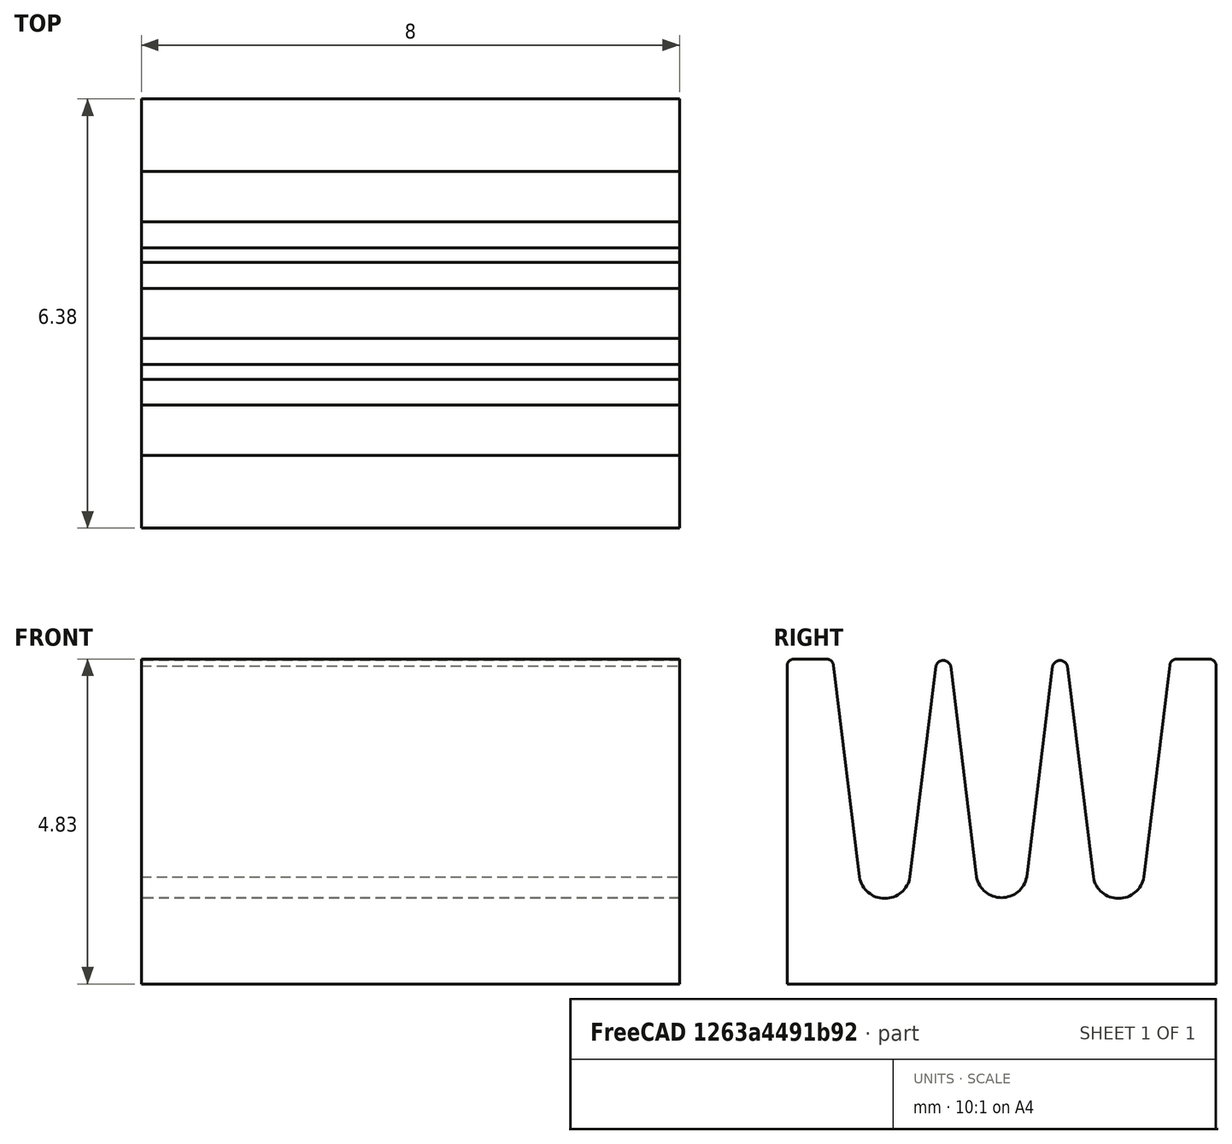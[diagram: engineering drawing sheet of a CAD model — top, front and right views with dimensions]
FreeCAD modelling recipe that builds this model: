
FCSTD DOCUMENT  (FreeCAD 0.14R3702 (Git))
Label: heat-sink-8x6x5mm
License: CC-BY 3.0
LicenseURL: http://creativecommons.org/licenses/by/3.0/
objects: Sketcher::SketchObject×1, PartDesign::Pad×1
note: 3 computed .brp shape members not serialized (recipe doc carries the construction recipe); baked Part::Feature solids carry a one-line shape summary decoded from their .brp

FEATURE [Sketcher::SketchObject] Sketch  label="heat-sink-sketch"
  Placement = pos=(0,0,0) rot=(0.57735,0.57735,0.57735;2.0944rad)
  sketch-geometry (25):
    g0: LineSegment StartX=3.19 StartY=0 StartZ=0 EndX=-3.19 EndY=0 EndZ=0
    g1: LineSegment [constr] StartX=-3.18796 StartY=1.26 StartZ=0 EndX=0 EndY=1.26 EndZ=0
    g2: LineSegment [constr] StartX=-2.59925 StartY=4.83 StartZ=0 EndX=0 EndY=4.83 EndZ=0
    g3: LineSegment [constr] StartX=-1.73796 StartY=4.83 StartZ=0 EndX=-1.73796 EndY=1.26 EndZ=0
    g4: LineSegment [constr] StartX=-0.86796 StartY=4.83 StartZ=0 EndX=-0.86796 EndY=1.26 EndZ=0
    g5: LineSegment [constr] StartX=-2.11296 StartY=1.59 StartZ=0 EndX=-1.36296 EndY=1.59 EndZ=0
    g6: LineSegment StartX=-2.5 StartY=4.74219 StartZ=0 EndX=-2.11296 EndY=1.59 EndZ=0
    g7: LineSegment StartX=-0.97796 StartY=4.72557 StartZ=0 EndX=-1.36296 EndY=1.59 EndZ=0
    g8: LineSegment StartX=-0.75796 StartY=4.72557 StartZ=0 EndX=-0.37296 EndY=1.59 EndZ=0
    g9: LineSegment StartX=0.75796 StartY=4.72557 StartZ=0 EndX=0.37296 EndY=1.59 EndZ=0
    g10: ArcOfCircle CenterX=-1.73796 CenterY=1.65144 CenterZ=0 NormalX=0 NormalY=0 NormalZ=1 Radius=0.38 StartAngle=3.30399 EndAngle=6.12079
    g11: ArcOfCircle CenterX=-0.86796 CenterY=4.69564 CenterZ=0 NormalX=0 NormalY=0 NormalZ=1 Radius=0.114 StartAngle=0.265687 EndAngle=2.87591
    g12: LineSegment StartX=-3.19 StartY=0 StartZ=0 EndX=-3.19 EndY=4.73 EndZ=0
    g13: LineSegment StartX=-3.09 StartY=4.83 StartZ=0 EndX=-2.59925 EndY=4.83 EndZ=0
    g14: ArcOfCircle CenterX=-3.09 CenterY=4.73 CenterZ=0 NormalX=0 NormalY=0 NormalZ=1 Radius=0.1 StartAngle=1.5708 EndAngle=3.14159
    g15: ArcOfCircle CenterX=-2.59925 CenterY=4.73 CenterZ=0 NormalX=0 NormalY=0 NormalZ=1 Radius=0.1 StartAngle=0.122173 EndAngle=1.5708
    g16: ArcOfCircle CenterX=0 CenterY=1.66281 CenterZ=0 NormalX=0 NormalY=0 NormalZ=1 Radius=0.38 StartAngle=3.33438 EndAngle=6.0904
    g17: LineSegment StartX=0.97796 StartY=4.72557 StartZ=0 EndX=1.36296 EndY=1.59 EndZ=0
    g18: LineSegment StartX=2.11296 StartY=1.59 StartZ=0 EndX=2.5 EndY=4.74219 EndZ=0
    g19: LineSegment StartX=3.19 StartY=4.73 StartZ=0 EndX=3.19 EndY=0 EndZ=0
    g20: LineSegment StartX=2.59925 StartY=4.83 StartZ=0 EndX=3.09 EndY=4.83 EndZ=0
    g21: ArcOfCircle CenterX=0.86796 CenterY=4.69564 CenterZ=0 NormalX=0 NormalY=0 NormalZ=1 Radius=0.114 StartAngle=0.265687 EndAngle=2.87591
    g22: ArcOfCircle CenterX=1.73796 CenterY=1.65144 CenterZ=0 NormalX=0 NormalY=0 NormalZ=1 Radius=0.38 StartAngle=3.30399 EndAngle=6.12079
    g23: ArcOfCircle CenterX=2.59925 CenterY=4.73 CenterZ=0 NormalX=0 NormalY=0 NormalZ=1 Radius=0.1 StartAngle=1.5708 EndAngle=3.01942
    g24: ArcOfCircle CenterX=3.09 CenterY=4.73 CenterZ=0 NormalX=0 NormalY=0 NormalZ=1 Radius=0.1 StartAngle=0 EndAngle=1.5708
  constraints (71):
    c: Symmetric(g0,g0,g-2)
    c: PointOnObject(g0,g-1)
    c: DistanceX(g0) = -6.38
    c: Horizontal(g1)
    c: PointOnObject(g1,g-2)
    c: DistanceY(g-1,g1) = 1.26
    c: PointOnObject(g2,g-2)
    c: PointOnObject(g3,g2)
    c: PointOnObject(g3,g1)
    c: DistanceX(g1,g3) = 1.45
    c: PointOnObject(g4,g1)
    c: PointOnObject(g4,g2)
    c: DistanceX(g3,g4) = 0.87
    c: DistanceX(g3,g4) = 0.87
    c: Horizontal(g5)
    c: Angle(g6,g2) = 1.44862
    c: Angle(g2,g7) = 1.44862
    c: Coincident(g5,g7)
    c: Coincident(g5,g6)
    c: Symmetric(g5,g5,g3)
    c: DistanceX(g5) = 0.75
    c: DistanceY(g5,g4) = -0.33
    c: Parallel(g8,g6)
    c: Symmetric(g7,g8,g4)
    c: DistanceX(g7,g8) = 0.22
    c: Symmetric(g8,g5,g4)
    c: Symmetric(g8,g9,g-2)
    c: Symmetric(g9,g8,g-2)
    c: Coincident(g10,g5)
    c: Coincident(g10,g5)
    c: Radius(g10) = 0.38
    c: Coincident(g11,g7)
    c: Coincident(g11,g8)
    c: Radius(g11) = 0.114
    c: DistanceY(g2,g0) = -4.83
    c: Vertical(g12)
    c: Horizontal(g13)
    c: Coincident(g12,g0)
    c: Tangent(g12,g14)
    c: Tangent(g13,g14)
    c: Radius(g14) = 0.1
    c: Tangent(g6,g15)
    c: Tangent(g13,g15)
    c: Equal(g15,g14)
    c: DistanceX(g12,g6) = 0.69
    c: Coincident(g2,g13)
    c: Coincident(g16,g8)
    c: Coincident(g16,g9)
    c: Equal(g10,g16)
    c: Symmetric(g5,g17,g-2)
    c: Symmetric(g17,g7,g-2)
    c: Symmetric(g18,g6,g-2)
    c: Symmetric(g18,g5,g-2)
    c: Vertical(g19)
    c: Coincident(g19,g0)
    c: Symmetric(g19,g12,g-2)
    c: Horizontal(g20)
    c: Symmetric(g20,g2,g-2)
    c: Symmetric(g20,g13,g-2)
    c: Coincident(g21,g9)
    c: Coincident(g17,g21)
    c: Equal(g21,g11)
    c: Equal(g22,g16)
    c: Coincident(g22,g17)
    c: Coincident(g22,g18)
    c: Equal(g23,g14)
    c: Coincident(g23,g18)
    c: Coincident(g23,g20)
    c: Coincident(g24,g20)
    c: Coincident(g24,g19)
    c: Equal(g24,g23)
FEATURE [PartDesign::Pad] Pad  label="heat-sink-8x6x5mm"
  Length = 8
  Length2 = 100
  Midplane = true
  Placement = pos=(0,0,0) rot=(0.57735,0.57735,0.57735;2.0944rad)
  Sketch = -> Sketch
  Type = 0
